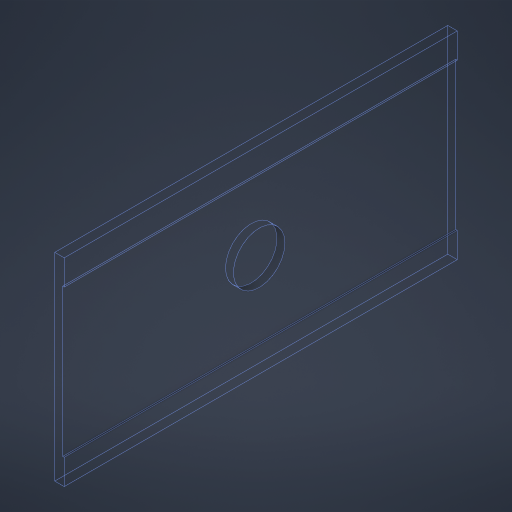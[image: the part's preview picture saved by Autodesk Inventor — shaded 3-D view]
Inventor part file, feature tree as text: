
AUTODESK INVENTOR PART (.ipt)
format: ipt  version: 2024 (Build 280153000, 153)  size: 218,112 bytes
history: native  units: mm
features: extrude x3, sketch x3
ambient origin geometry x8: Origin, YZ Plane, XZ Plane, XY Plane, X Axis, Y Axis, Z Axis, Center Point
bodies: Solid1 (feature_tree)
feature tree (6):
  extrude  "Extrusion1"  Depth=496.0mm
  extrude  "Extrusion3"  Depth=32.0mm
  extrude  "Extrusion4"  Depth=186.0mm
  sketch  "Sketch1"  dims[d0=10.0mm d1=496.0mm]
  sketch  "Sketch2"  dims[d2=250.0mm d3=0.0mm d4=32.0mm]
  sketch  "Sketch3"  dims[d5=32.0mm d6=186.0mm d9=2.0mm d10=0.0mm d11=65.0mm d12=35.0mm d13=0.0mm]
